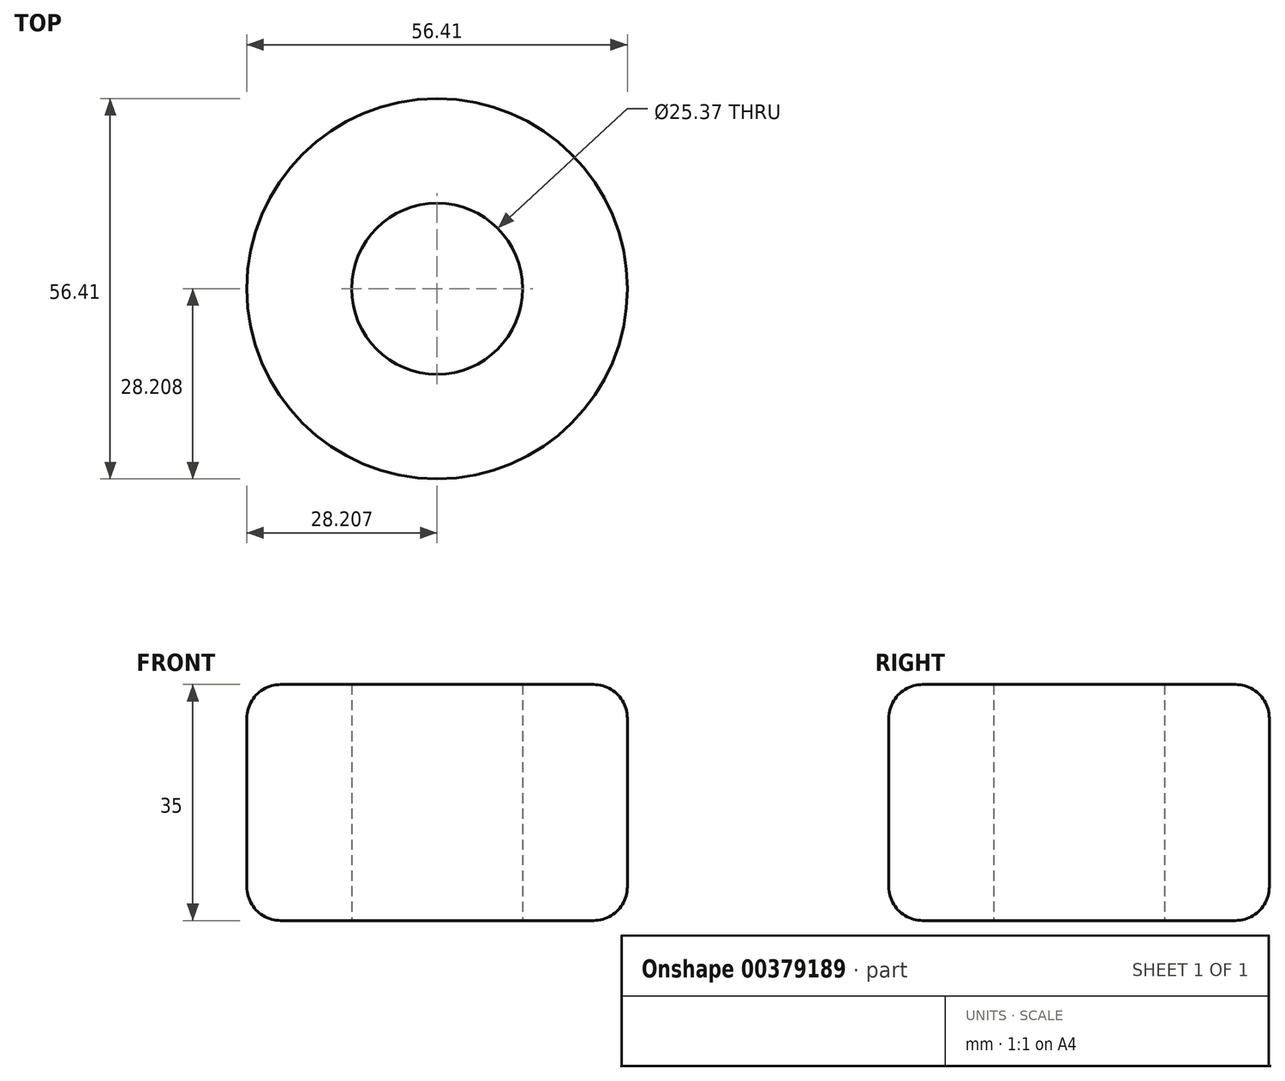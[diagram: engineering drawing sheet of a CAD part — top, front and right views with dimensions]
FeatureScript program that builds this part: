
annotation { "Feature Type Name" : "Feature", "Feature Type Description" : "" }
export const myFeature = defineFeature(function(context is Context, id is Id, definition is map)
    precondition{}
    {
        {
            var Q0;
            Q0=qCreatedBy(makeId("Top.planeOp"),FACE);
            var sketch = newSketch(context, id + "F0", { "sketchPlane" : qUnion([Q0])});
            skCircle(sketch, "E0", {"center": v(-6.71, 6.05) * mm, "radius": 28.2 * mm});
            skCircle(sketch, "E1", {"center": v(-6.71, 6.05) * mm, "radius": 12.69 * mm});
            skSolve(sketch);
        }
        {
            var Q0;
            Q0 = qSketchRegion(id + "F0", true);
            extrude(context, id + "F1", {"entities" : qUnion([Q0]), "depth" : 35 * mm, "offsetDistance" : 25 * mm});
        }
        {
            var Q0;
            Q0=makeQuery(id+"F1.opExtrude","SWEPT_FACE",FACE,{"disambiguationData":[OSD([sQuery(id+"F0.wireOp",EDGE,"E0")])]});
            fillet(context, id + "F2", {"entities" : qUnion([Q0]), "tangentPropagation" : true, "radius" : 5 * mm, "defaultsChanged" : false, "vertexSettings" : [], "allowEdgeOverflow" : false});
        }
    });
